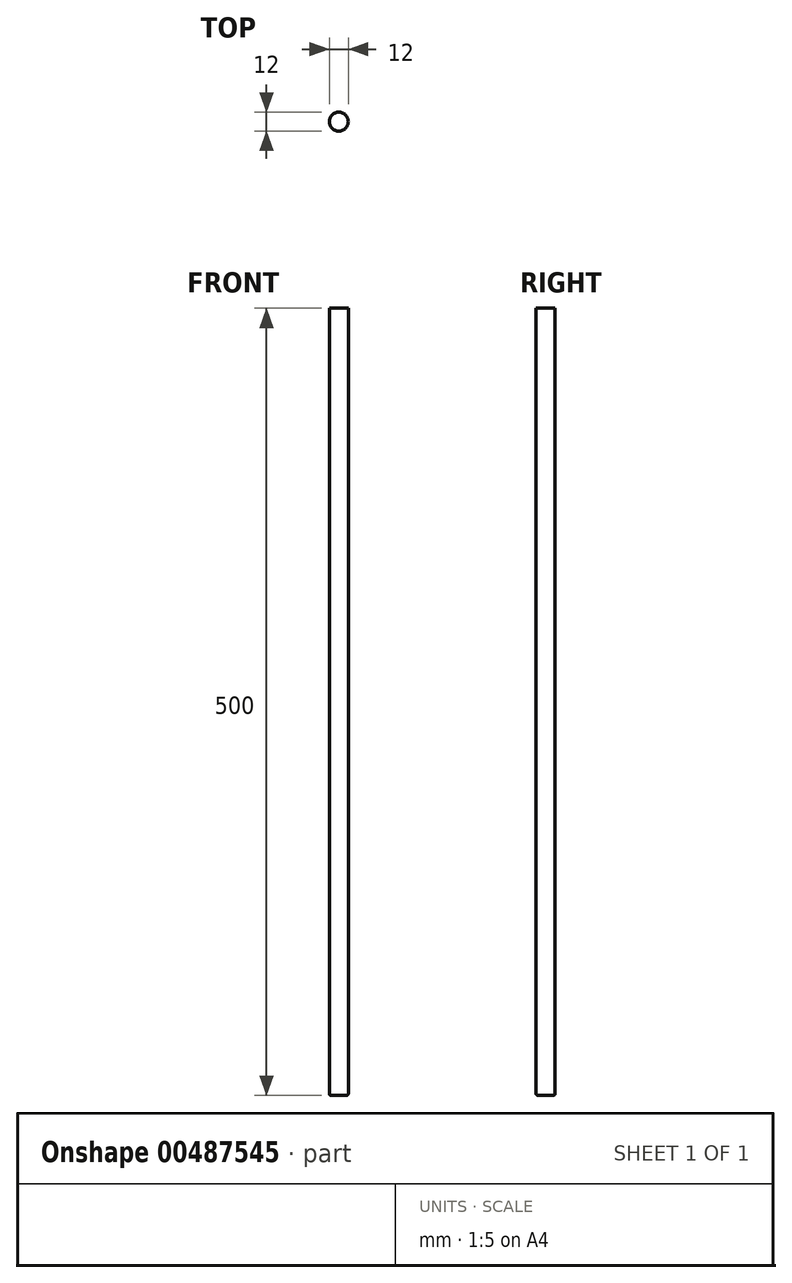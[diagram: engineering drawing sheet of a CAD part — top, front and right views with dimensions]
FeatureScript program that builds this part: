
annotation { "Feature Type Name" : "Feature", "Feature Type Description" : "" }
export const myFeature = defineFeature(function(context is Context, id is Id, definition is map)
    precondition{}
    {
        {
            var Q0;
            Q0=qCreatedBy(makeId("Top.planeOp"),FACE);
            var sketch = newSketch(context, id + "F0", { "sketchPlane" : qUnion([Q0])});
            skCircle(sketch, "E0", {"center": v(0, 0) * mm, "radius": 6 * mm});
            skSolve(sketch);
        }
        {
            var Q0;
            Q0=makeQuery(id+"F0.imprint","IMPRINT",FACE,{"disambiguationData":[TD([[makeQuery(id+"F0.imprint","IMPRINT",EDGE,{"derivedFrom":sQuery(id+"F0.wireOp",EDGE,"E0")}),1.0]])]});
            var Q1;
            Q1=sQuery(id+"F0.wireOp",EDGE,"E0");
            extrude(context, id + "F1", {"entities" : qUnion([Q0]), "surfaceEntities" : qUnion([Q1]), "depth" : 500 * mm, "offsetDistance" : 25 * mm});
        }
        {
            var Q0;
            Q0=makeQuery(id+"F1.opExtrude","CAP_EDGE",EDGE,{"disambiguationData":[OSD([sQuery(id+"F0.wireOp",EDGE,"E0")])],"isStart":true});
            fillet(context, id + "F2", {"entities" : qUnion([Q0]), "radius" : 1 * mm, "tangentPropagation" : true, "allowEdgeOverflow" : false});
        }
    });
